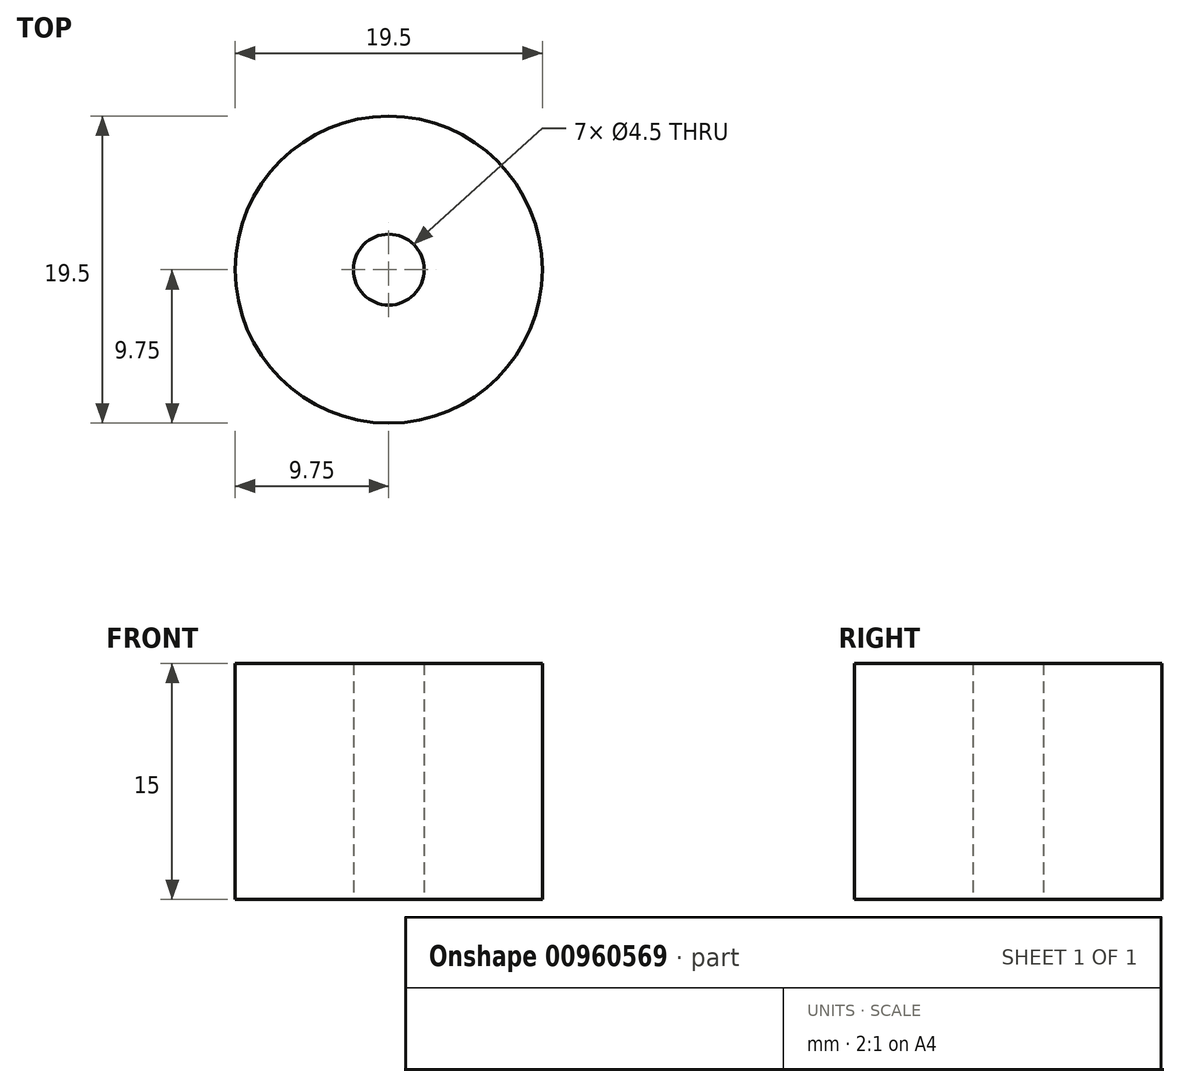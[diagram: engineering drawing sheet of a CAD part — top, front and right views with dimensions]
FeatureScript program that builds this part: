
annotation { "Feature Type Name" : "Feature", "Feature Type Description" : "" }
export const myFeature = defineFeature(function(context is Context, id is Id, definition is map)
    precondition{}
    {
        {
            var Q0;
            Q0=qCreatedBy(makeId("Top.planeOp"),FACE);
            var sketch = newSketch(context, id + "F0", { "sketchPlane" : qUnion([Q0])});
            skCircle(sketch, "E0", {"center": v(0, 0) * mm, "radius": 9.75 * mm});
            skCircle(sketch, "E1", {"center": v(0, 0) * mm, "radius": 2.25 * mm});
            skSolve(sketch);
        }
        {
            var Q0;
            Q0=makeQuery(id+"F0.imprint","IMPRINT",FACE,{"disambiguationData":[TD([[makeQuery(id+"F0.imprint","IMPRINT",EDGE,{"derivedFrom":sQuery(id+"F0.wireOp",EDGE,"E0")}),1.0]])]});
            extrude(context, id + "F1", {"entities" : qUnion([Q0]), "depth" : 15 * mm, "offsetDistance" : 25 * mm});
        }
    });
